# Revit family: FP-Revit20-en-RB6018BRV-0-90005323A-NZ-AU
name_source: partatom
category: Specialty Equipment
units: mm (PartAtom-declared; Revit-internal decimal feet)

## family parameters
Always vertical = No
Cut with Voids When Loaded = Yes
Part Type = Normal
Room Calculation Point = No
Round Connector Dimension = Use Diameter
Shared = No
Work Plane-Based = Yes

## types (1)
- RB6018BRV
    Cavity - Depth = 560 mm  [stored 1.83727 ft]
    Cavity - Height = 1778 mm  [stored 5.83333 ft]
    Cavity - Width = 560 mm  [stored 1.83727 ft]
    Connector Description - Electrical = 230 V, 50 Hz, 10 A
    Default Elevation = 0 mm  [stored 0 ft]
    Description = 60cm Series 5 Integrated Refrigerator Freezer
    Manufacturer = Fisher & Paykel Appliances
    Material - Clearance required = Fisher & Paykel - Clearance Required
    Material - Custom Panel = Oak, White
    Model = RB6018BRV
    Product - Depth = 550 mm
    Product - Height = 1772 mm  [stored 5.81365 ft]
    Product - Width = 550 mm
    URL = www.fisherpaykel.com
    Visibility - Custom Panel = Yes

note: [stored X ft] marks values corroborated as IEEE doubles in the binary element streams (Revit-internal decimal feet)

## geometry (parser evidence)
native form markers: Sweep x19
no freeform markers — native parametric forms only
